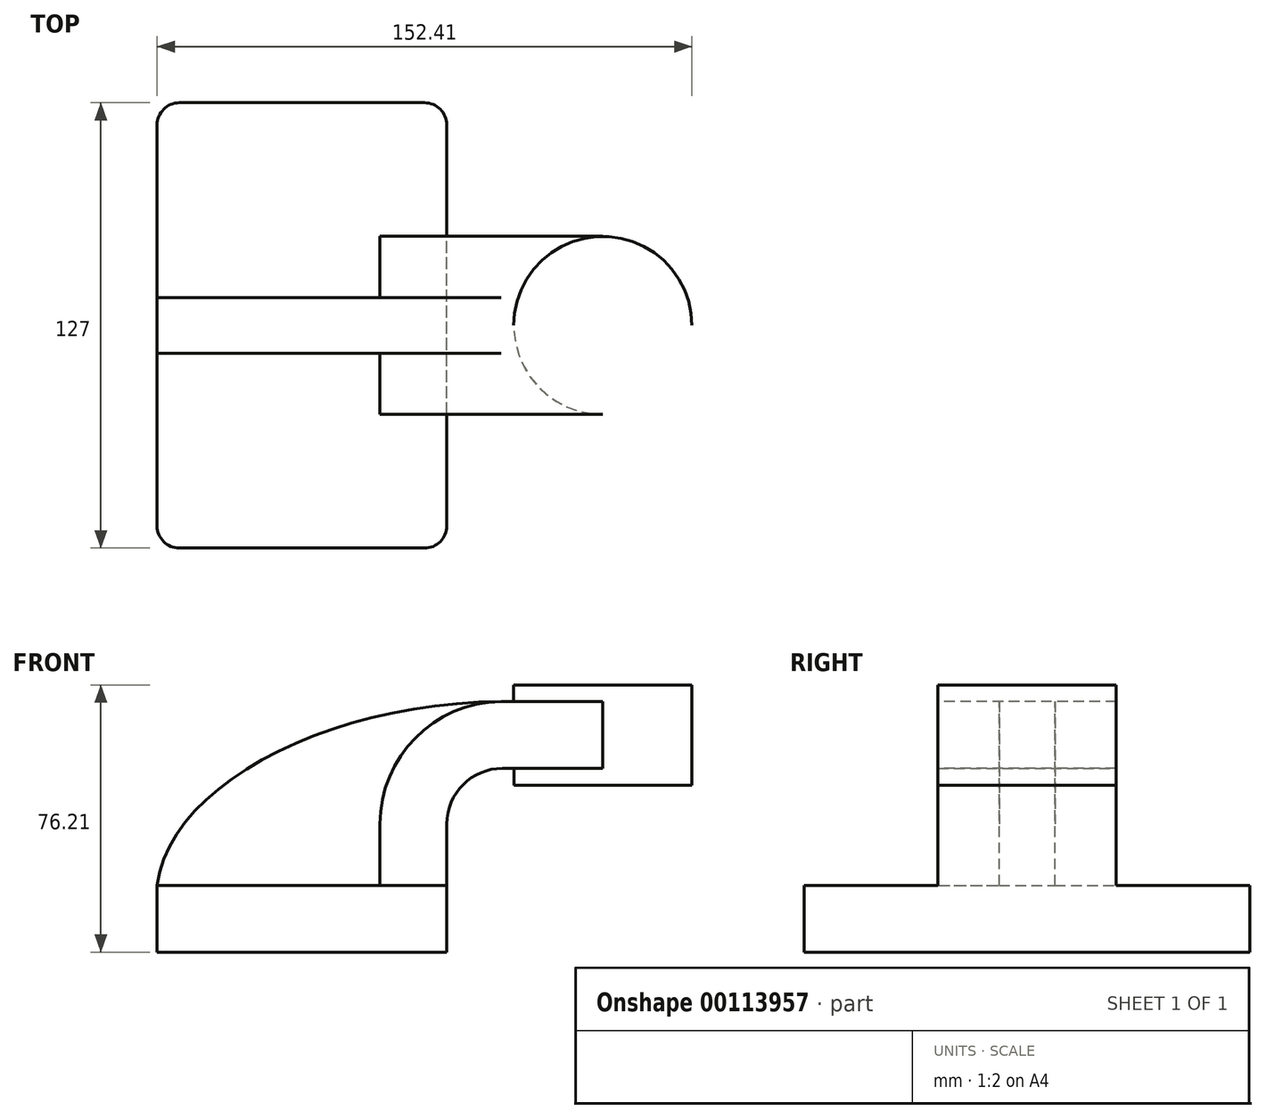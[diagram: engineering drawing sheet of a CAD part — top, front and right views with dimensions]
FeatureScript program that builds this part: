
annotation { "Feature Type Name" : "Feature", "Feature Type Description" : "" }
export const myFeature = defineFeature(function(context is Context, id is Id, definition is map)
    precondition{}
    {
        {
            var Q0;
            Q0=qCreatedBy(makeId("Front.planeOp"),FACE);
            var sketch = newSketch(context, id + "F0", { "sketchPlane" : qUnion([Q0])});
            skLineSegment(sketch, "E0.bottom", {"start": v(-41.28, 9.53) * mm, "end": v(41.28, 9.53) * mm});
            skLineSegment(sketch, "E0.top", {"start": v(-41.28, -9.53) * mm, "end": v(41.28, -9.53) * mm});
            skLineSegment(sketch, "E0.left", {"start": v(-41.28, 9.53) * mm, "end": v(-41.28, -9.53) * mm});
            skLineSegment(sketch, "E0.right", {"start": v(41.28, 9.53) * mm, "end": v(41.28, -9.53) * mm});
            skPoint(sketch, "E0.middle", {"position": v(0, 0) * mm});
            skLineSegment(sketch, "E1.bottom", {"start": v(111.13, 38.1) * mm, "end": v(60.33, 38.1) * mm});
            skLineSegment(sketch, "E1.top", {"start": v(111.13, 66.68) * mm, "end": v(60.33, 66.68) * mm});
            skLineSegment(sketch, "E1.left", {"start": v(111.13, 38.1) * mm, "end": v(111.13, 66.68) * mm});
            skLineSegment(sketch, "E1.right", {"start": v(60.33, 38.1) * mm, "end": v(60.33, 66.68) * mm});
            skPoint(sketch, "E1.middle", {"position": v(85.73, 52.39) * mm});
            skLineSegment(sketch, "E2", {"start": v(41.28, 9.53) * mm, "end": v(41.28, 27) * mm});
            skArc(sketch, "E3", {"start": v(41.28, 27) * mm, "mid": v(45.92, 38.23) * mm, "end": v(57.15, 42.88) * mm});
            skLineSegment(sketch, "E4", {"start": v(57.15, 42.88) * mm, "end": v(85.75, 42.88) * mm});
            skLineSegment(sketch, "E5.0", {"start": v(57.15, 61.93) * mm, "end": v(85.73, 61.93) * mm});
            skArc(sketch, "E5.1", {"start": v(22.23, 27) * mm, "mid": v(32.45, 51.7) * mm, "end": v(57.15, 61.93) * mm});
            skLineSegment(sketch, "E5.2", {"start": v(22.23, 9.53) * mm, "end": v(22.23, 27) * mm});
            skLineSegment(sketch, "E6", {"start": v(85.73, 66.68) * mm, "end": v(85.75, 38.1) * mm});
            skPoint(sketch, "E6.endSnap0", {"position": v(85.73, 38.1) * mm});
            skFitSpline(sketch, "E7", {"points": [v(-41.28, 9.53) * mm, v(57.15, 61.93) * mm], "startDerivative": vector(11.6, 87.48) * mm, "endDerivative": vector(146.88, 0.65) * mm});
            skSolve(sketch);
        }
        {
            var Q0;
            Q0=makeQuery(id+"F0.imprint","IMPRINT",FACE,{"disambiguationData":[TD([[makeQuery(id+"F0.imprint","IMPRINT",EDGE,{"derivedFrom":sQuery(id+"F0.wireOp",EDGE,"E0.top")}),1.0]])]});
            extrude(context, id + "F1", {"entities" : qUnion([Q0]), "endBound" : BoundingType.SYMMETRIC, "depth" : 127 * mm});
        }
        {
            var Q0;
            {var subQ1=sQuery(id+"F0.wireOp",EDGE,"E2");Q0=makeQuery(id+"F0.imprint","IMPRINT",FACE,{"disambiguationData":[TD([[makeQuery(id+"F0.imprint","IMPRINT",EDGE,{"derivedFrom":subQ1}),1.0]])]});}
            var Q1;
            {var subQ0=sQuery(id+"F0.wireOp",EDGE,"E4");var subQ1=sQuery(id+"F0.wireOp",EDGE,"E1.right");var subQ2=makeQuery(id+"F0.imprint","INTERSECT",VERTEX,{"derivedFrom":[subQ1,subQ0]});Q1=makeQuery(id+"F0.imprint","IMPRINT",FACE,{"disambiguationData":[TD([[makeQuery(id+"F0.imprint","IMPRINT",EDGE,{"disambiguationData":[TD([[subQ2,-1.0]])],"derivedFrom":subQ1}),-1.0]])]});}
            extrude(context, id + "F2", {"entities" : qUnion([Q0, Q1]), "operationType" : NewBodyOperationType.ADD, "endBound" : BoundingType.SYMMETRIC, "depth" : 50.8 * mm});
        }
        {
            var Q0;
            {var subQ3=sQuery(id+"F0.wireOp",EDGE,"E5.2");Q0=makeQuery(id+"F0.imprint","IMPRINT",FACE,{"disambiguationData":[TD([[makeQuery(id+"F0.imprint","IMPRINT",EDGE,{"derivedFrom":subQ3}),1.0]])]});}
            extrude(context, id + "F3", {"entities" : qUnion([Q0]), "operationType" : NewBodyOperationType.ADD, "endBound" : BoundingType.SYMMETRIC, "depth" : 15.88 * mm});
        }
        {
            var Q0;
            {var subQ0=sQuery(id+"F0.wireOp",EDGE,"E1.left");Q0=makeQuery(id+"F0.imprint","IMPRINT",FACE,{"disambiguationData":[TD([[makeQuery(id+"F0.imprint","IMPRINT",EDGE,{"derivedFrom":subQ0}),1.0]])]});}
            var Q1;
            Q1=sQuery(id+"F0.wireOp",EDGE,"E6");
            revolve(context, id + "F4", {"operationType" : NewBodyOperationType.ADD, "entities" : qUnion([Q0]), "axis" : qUnion([Q1]), "revolveType" : RevolveType.FULL});
        }
        {
            var Q0;
            Q0=makeQuery(id+"F1.opExtrude","CAP_EDGE",EDGE,{"disambiguationData":[OSD([sQuery(id+"F0.wireOp",EDGE,"E0.right")])],"isStart":true});
            var Q1;
            Q1=makeQuery(id+"F1.opExtrude","CAP_EDGE",EDGE,{"disambiguationData":[OSD([sQuery(id+"F0.wireOp",EDGE,"E0.right")])],"isStart":false});
            var Q2;
            Q2=makeQuery(id+"F1.opExtrude","CAP_EDGE",EDGE,{"disambiguationData":[OSD([sQuery(id+"F0.wireOp",EDGE,"E0.left")])],"isStart":true});
            var Q3;
            Q3=makeQuery(id+"F1.opExtrude","CAP_EDGE",EDGE,{"disambiguationData":[OSD([sQuery(id+"F0.wireOp",EDGE,"E0.left")])],"isStart":false});
            fillet(context, id + "F5", {"entities" : qUnion([Q0, Q1, Q2, Q3]), "radius" : 6.35 * mm, "tangentPropagation" : true, "allowEdgeOverflow" : false});
        }
    });
